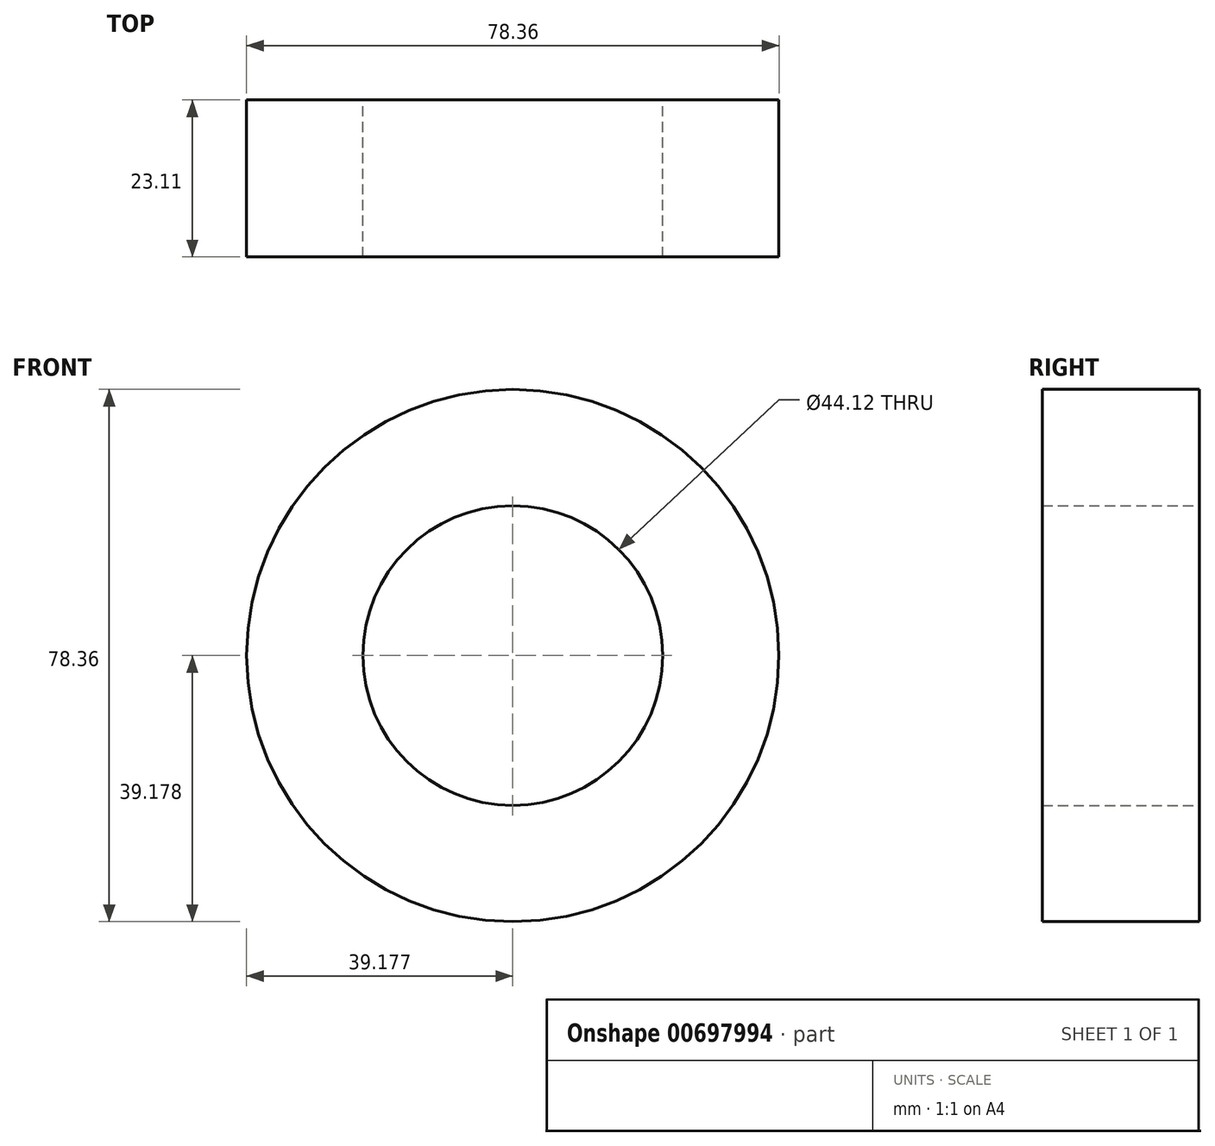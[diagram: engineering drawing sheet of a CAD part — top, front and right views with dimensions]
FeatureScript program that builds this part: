
annotation { "Feature Type Name" : "Feature", "Feature Type Description" : "" }
export const myFeature = defineFeature(function(context is Context, id is Id, definition is map)
    precondition{}
    {
        {
            var Q0;
            Q0=qCreatedBy(makeId("Front.planeOp"),FACE);
            var sketch = newSketch(context, id + "F0", { "sketchPlane" : qUnion([Q0])});
            skCircle(sketch, "E0", {"center": v(24.26, 196.5) * mm, "radius": 22.06 * mm});
            skCircle(sketch, "E1", {"center": v(24.26, 196.5) * mm, "radius": 39.18 * mm});
            skSolve(sketch);
        }
        {
            var Q0;
            Q0 = qSketchRegion(id + "F0", true);
            extrude(context, id + "F1", {"entities" : qUnion([Q0]), "depth" : 23.1 * mm, "offsetDistance" : 25.4 * mm});
        }
    });
